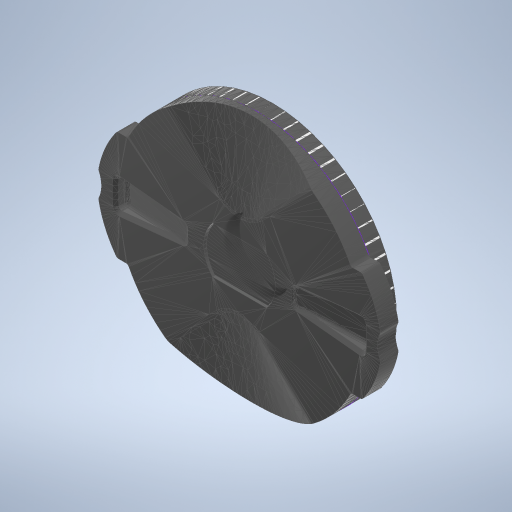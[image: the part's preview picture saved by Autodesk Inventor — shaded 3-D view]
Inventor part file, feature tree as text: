
AUTODESK INVENTOR PART (.ipt)
format: ipt  version: 2023 (Build 270158000, 158)  size: 363,520 bytes
history: native  units: in
note: dims shown in document units (in); Inventor stores cm internally (conversion verified against a paired STEP export)
features: other x2, sketch x2, extrude x2, plane x1
ambient origin geometry x8: Origin, YZ Plane, XZ Plane, XY Plane, X Axis, Y Axis, Z Axis, Center Point
bodies: Solid1 (feature_tree)
feature tree (7):
  other  "GarminQuarterTurn"
  plane  "Work Plane2"
  sketch  "Sketch2"  dims[d1=1.5in d2=0.0in d3=10.0in d4=0.0in]
  extrude  "Extrusion1"  Depth=1.5in TaperAngle=0.0deg
  extrude  "Extrusion2"  [1 undecoded]
  sketch  "Sketch3"
  other  "MeshFeature1"
note: 1 required parameter value undecoded (feature->parameter linkage not recoverable at this tier; creation-order binding heuristic only, values carry confidence <= 0.55)
